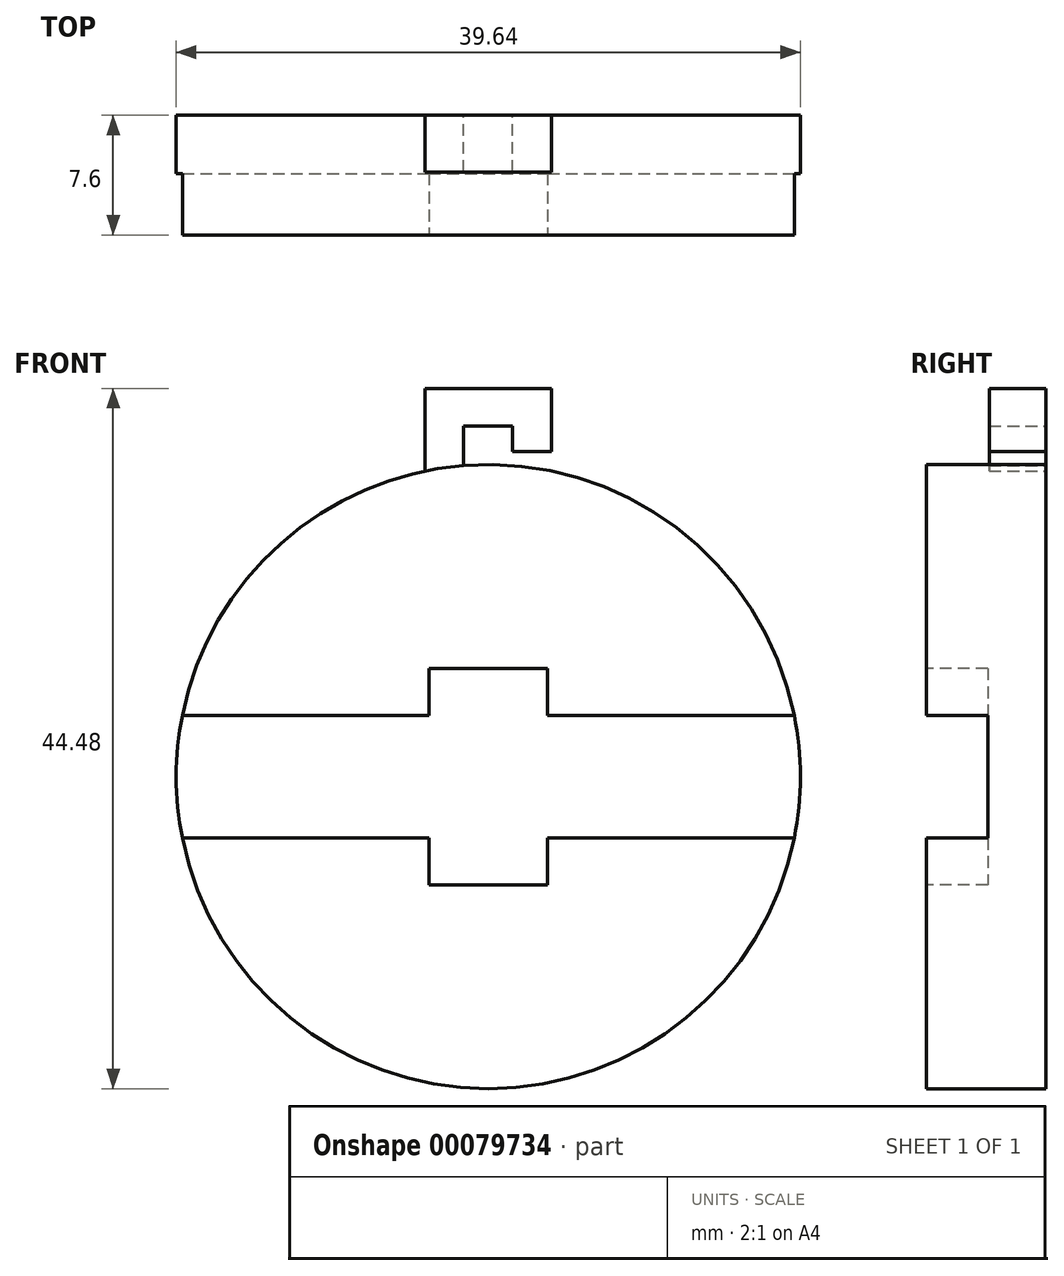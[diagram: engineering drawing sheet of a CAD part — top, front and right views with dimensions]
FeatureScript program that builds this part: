
annotation { "Feature Type Name" : "Feature", "Feature Type Description" : "" }
export const myFeature = defineFeature(function(context is Context, id is Id, definition is map)
    precondition{}
    {
        {
            var Q0;
            Q0=qCreatedBy(makeId("Front.planeOp"),FACE);
            var sketch = newSketch(context, id + "F0", { "sketchPlane" : qUnion([Q0])});
            skCircle(sketch, "E0", {"center": v(0, 0) * mm, "radius": 19.82 * mm});
            skSolve(sketch);
        }
        {
            var Q0;
            Q0 = qSketchRegion(id + "F0", true);
            extrude(context, id + "F1", {"entities" : qUnion([Q0]), "depth" : 7.6 * mm});
        }
        {
            var Q0;
            Q0=makeQuery(id+"F1.opExtrude","CAP_FACE",FACE,{"disambiguationData":[OSD([sQuery(id+"F0.wireOp",EDGE,"E0")])],"isStart":false});
            var sketch = newSketch(context, id + "F2", { "sketchPlane" : qUnion([Q0])});
            skLineSegment(sketch, "E1.bottom", {"start": v(-21.09, 3.9) * mm, "end": v(-3.78, 3.9) * mm});
            skLineSegment(sketch, "E1.top", {"start": v(-21.09, -3.9) * mm, "end": v(-3.78, -3.9) * mm});
            skLineSegment(sketch, "E1.left", {"start": v(-21.09, 3.9) * mm, "end": v(-21.09, -3.9) * mm});
            skLineSegment(sketch, "E1.right", {"start": v(21.09, 3.9) * mm, "end": v(21.09, -3.9) * mm});
            skPoint(sketch, "E1.middle", {"position": v(0, 0) * mm});
            skLineSegment(sketch, "E2.bottom", {"start": v(-3.77, 6.88) * mm, "end": v(3.78, 6.88) * mm});
            skLineSegment(sketch, "E2.top", {"start": v(-3.78, -6.88) * mm, "end": v(3.77, -6.88) * mm});
            skLineSegment(sketch, "E2.left", {"start": v(-3.77, 6.88) * mm, "end": v(-3.77, 3.9) * mm});
            skLineSegment(sketch, "E2.right", {"start": v(3.78, 6.88) * mm, "end": v(3.78, 3.9) * mm});
            skLineSegment(sketch, "E3.trimOffspring", {"start": v(-3.78, -3.9) * mm, "end": v(-3.78, -6.88) * mm});
            skLineSegment(sketch, "E4.trimOffspring", {"start": v(3.78, 3.9) * mm, "end": v(21.09, 3.9) * mm});
            skLineSegment(sketch, "E5.trimOffspring", {"start": v(3.78, -3.9) * mm, "end": v(3.77, -6.88) * mm});
            skLineSegment(sketch, "E6.trimOffspring", {"start": v(3.78, -3.9) * mm, "end": v(21.09, -3.9) * mm});
            skSolve(sketch);
        }
        {
            var Q0;
            Q0 = qSketchRegion(id + "F2", true);
            extrude(context, id + "F3", {"entities" : qUnion([Q0]), "operationType" : NewBodyOperationType.REMOVE, "oppositeDirection" : true, "depth" : 3.9 * mm});
        }
        {
            var Q0;
            Q0=qCreatedBy(makeId("Front.planeOp"),FACE);
            var sketch = newSketch(context, id + "F4", { "sketchPlane" : qUnion([Q0])});
            skLineSegment(sketch, "E7", {"start": v(0, -22.79) * mm, "end": v(0, 27.05) * mm, "construction": true});
            skLineSegment(sketch, "E8.bottom", {"start": v(4.02, 24.66) * mm, "end": v(-4.03, 24.66) * mm, "construction": true});
            skLineSegment(sketch, "E8.top", {"start": v(4.03, 19.4) * mm, "end": v(-4.03, 19.4) * mm, "construction": true});
            skLineSegment(sketch, "E8.left", {"start": v(4.03, 24.66) * mm, "end": v(4.03, 19.4) * mm, "construction": true});
            skLineSegment(sketch, "E8.right", {"start": v(-4.03, 24.66) * mm, "end": v(-4.03, 19.4) * mm, "construction": true});
            skLineSegment(sketch, "E9", {"start": v(-4.03, 19.4) * mm, "end": v(-4.03, 24.66) * mm});
            skLineSegment(sketch, "E10", {"start": v(4.03, 24.66) * mm, "end": v(-4.03, 24.66) * mm});
            skLineSegment(sketch, "E11", {"start": v(4.03, 24.66) * mm, "end": v(4.03, 20.66) * mm});
            skLineSegment(sketch, "E12", {"start": v(-4.03, 22.03) * mm, "end": v(-1.57, 22.03) * mm, "construction": true});
            skPoint(sketch, "E12.endSnap0", {"position": v(-4.03, 22.03) * mm});
            skLineSegment(sketch, "E13", {"start": v(-1.58, 22.26) * mm, "end": v(-1.58, 19.4) * mm});
            skLineSegment(sketch, "E14", {"start": v(-1.58, 24.66) * mm, "end": v(-1.58, 22.26) * mm, "construction": true});
            skLineSegment(sketch, "E15", {"start": v(-1.57, 22.26) * mm, "end": v(1.53, 22.26) * mm});
            skLineSegment(sketch, "E16", {"start": v(4.03, 20.66) * mm, "end": v(1.53, 20.66) * mm});
            skLineSegment(sketch, "E17", {"start": v(1.53, 20.66) * mm, "end": v(1.53, 22.26) * mm});
            skLineSegment(sketch, "E18", {"start": v(-4.03, 19.4) * mm, "end": v(-1.58, 19.4) * mm});
            skSolve(sketch);
        }
        {
            var Q0;
            Q0 = qSketchRegion(id + "F4", true);
            extrude(context, id + "F5", {"entities" : qUnion([Q0]), "operationType" : NewBodyOperationType.ADD, "depth" : 3.6 * mm});
        }
    });
